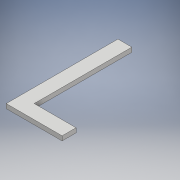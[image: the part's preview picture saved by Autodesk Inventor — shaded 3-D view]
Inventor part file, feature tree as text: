
AUTODESK INVENTOR PART (.ipt)
format: ipt  version: 2017 (Build 210142000, 142)  size: 98,304 bytes
history: native  units: mm
features: extrude x1, sketch x1
ambient origin geometry x8: Origin, YZ Plane, XZ Plane, XY Plane, X Axis, Y Axis, Z Axis, Center Point
bodies: Solid1 (feature_tree)
feature tree (2):
  extrude  "Extrusion1"  Depth=3.175mm
  sketch  "Sketch1"  dims[d0=10.0mm d1=35.0mm d2=80.0mm d3=35.0mm d4=5.0mm d5=40.0mm d6=3.175mm d7=0.0mm]
